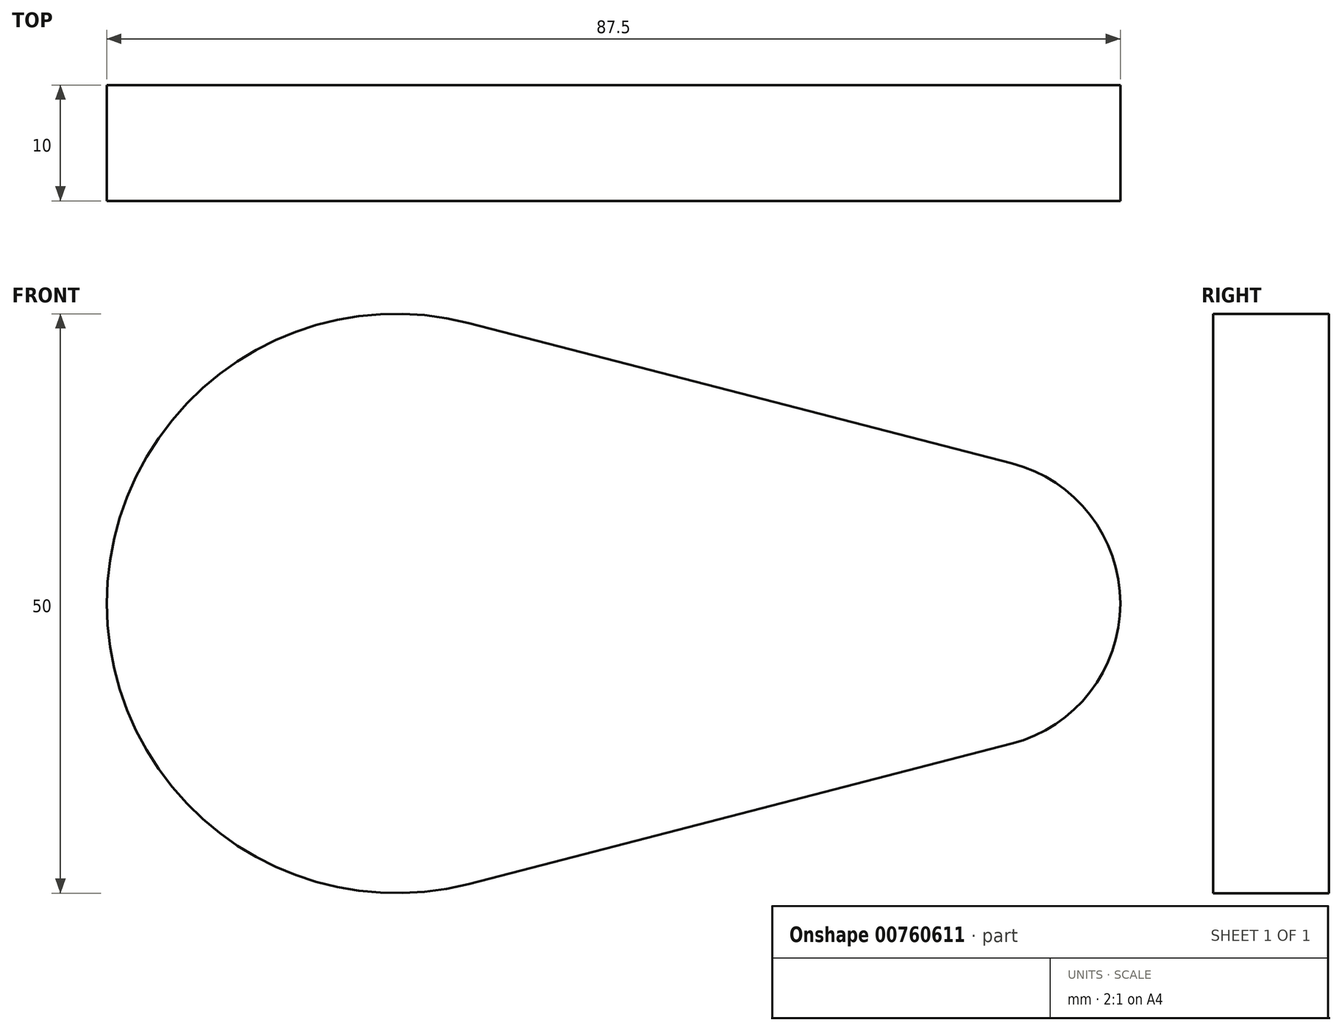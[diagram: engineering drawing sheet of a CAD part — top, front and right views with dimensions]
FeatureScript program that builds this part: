
annotation { "Feature Type Name" : "Feature", "Feature Type Description" : "" }
export const myFeature = defineFeature(function(context is Context, id is Id, definition is map)
    precondition{}
    {
        {
            var Q0;
            Q0=qCreatedBy(makeId("Front.planeOp"),FACE);
            var sketch = newSketch(context, id + "F0", { "sketchPlane" : qUnion([Q0])});
            skArc(sketch, "E0", {"start": v(-26.85, 24.2) * mm, "mid": v(-58.1, 0) * mm, "end": v(-26.85, -24.2) * mm});
            skArc(sketch, "E1", {"start": v(20.02, -12.1) * mm, "mid": v(29.4, 0) * mm, "end": v(20.02, 12.1) * mm});
            skLineSegment(sketch, "E2", {"start": v(-26.85, -24.2) * mm, "end": v(20.02, -12.1) * mm});
            skLineSegment(sketch, "E3", {"start": v(-26.85, 24.2) * mm, "end": v(20.02, 12.1) * mm});
            skCircle(sketch, "E4", {"center": v(16.9, 0) * mm, "radius": 12.5 * mm});
            skCircle(sketch, "E5", {"center": v(-33.1, 0) * mm, "radius": 25 * mm});
            skSolve(sketch);
        }
        {
            var Q0;
            Q0 = qSketchRegion(id + "F0", true);
            extrude(context, id + "F1", {"entities" : qUnion([Q0]), "depth" : 10 * mm, "offsetDistance" : 25 * mm});
        }
        {
            var Q0;
            Q0=sQuery(id+"F0.wireOp",EDGE,"E5");
            extrude(context, id + "F2", {"bodyType" : ToolBodyType.SURFACE, "surfaceEntities" : qUnion([Q0]), "depth" : 20 * mm, "offsetDistance" : 25 * mm});
        }
        {
            var Q0;
            Q0=sQuery(id+"F0.wireOp",EDGE,"E4");
            extrude(context, id + "F3", {"bodyType" : ToolBodyType.SURFACE, "surfaceEntities" : qUnion([Q0]), "depth" : 25 * mm, "offsetDistance" : 25 * mm});
        }
    });
